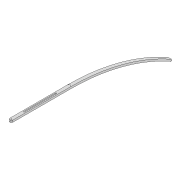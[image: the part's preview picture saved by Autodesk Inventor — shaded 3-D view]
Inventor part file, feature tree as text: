
AUTODESK INVENTOR PART (.ipt)
format: ipt  version: 2022 (Build 260153000, 153)  size: 121,856 bytes
history: native  units: mm
features: extrude x2, sketch x2, projected_geometry x2, fillet x1
ambient origin geometry x8: Origin, YZ Plane, XZ Plane, XY Plane, X Axis, Y Axis, Z Axis, Center Point
bodies: Solid1 (feature_tree)
feature tree (7):
  extrude  "Extrusion1"  Depth=10.0mm
  extrude  "Extrusion2"  Depth=2.0mm
  fillet  "Fillet1"  Radius=140.0mm
  sketch  "Sketch1"  dims[d0=180.0mm d1=10.0mm]
  sketch  "Sketch2"  dims[d2=3.3mm d3=40.0mm d5=140.0mm d6=3.3mm d7=6.0mm d8=0.0mm d9=6.0mm d10=498.004mm d11=90.0mm d12=10.0mm d13=0.0mm d14=2.0mm]
  projected_geometry  "Projected Loop1"
  projected_geometry  "Projected Loop2"
